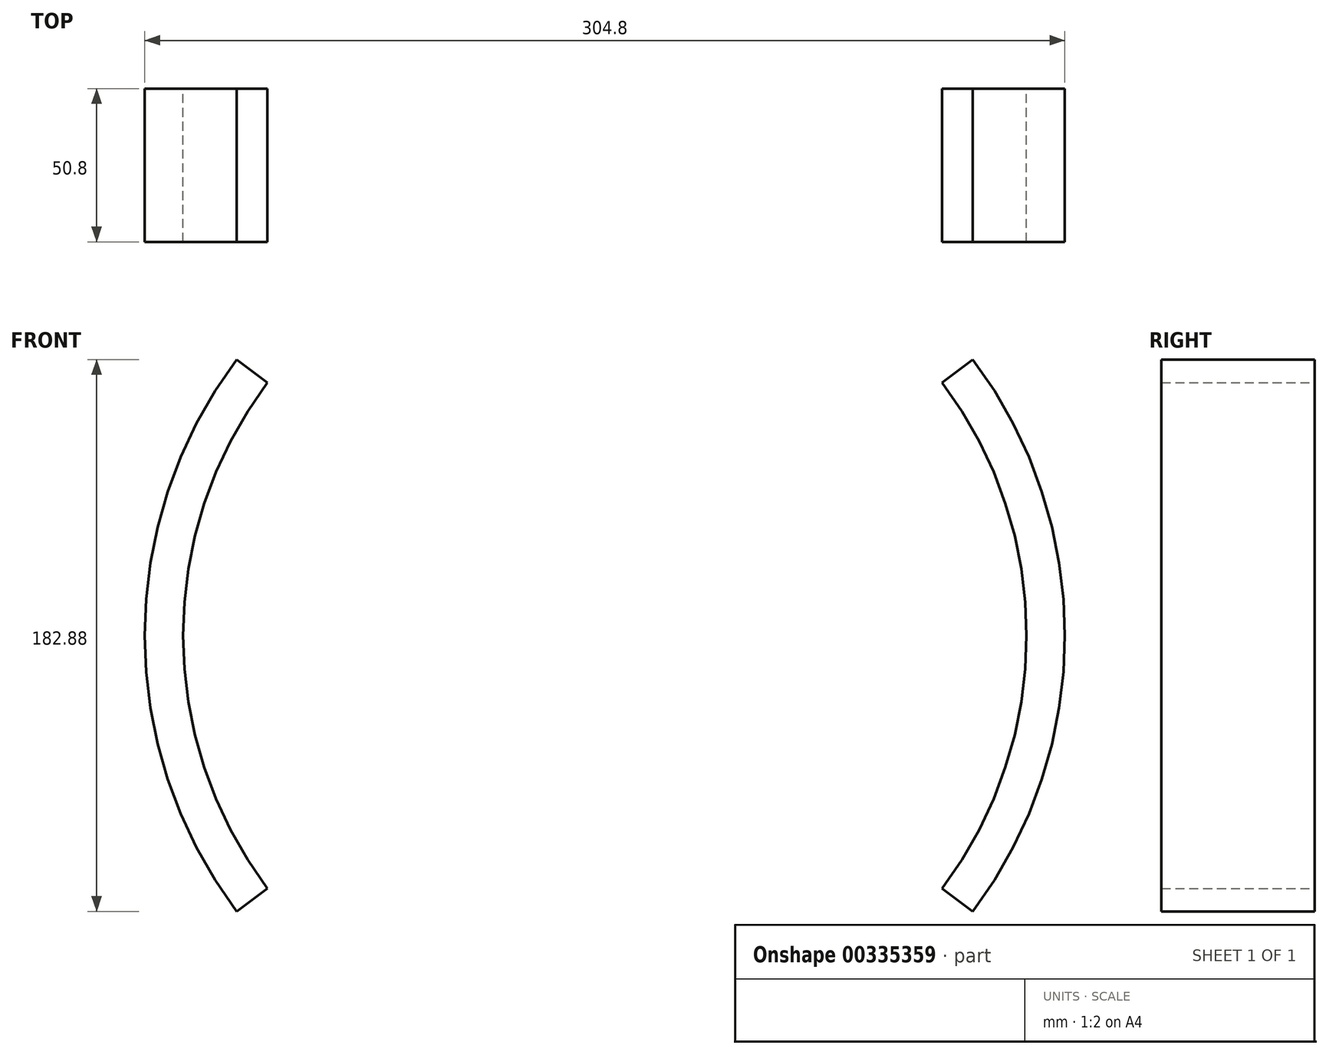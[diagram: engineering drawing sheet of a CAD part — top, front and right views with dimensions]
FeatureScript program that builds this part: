
annotation { "Feature Type Name" : "Feature", "Feature Type Description" : "" }
export const myFeature = defineFeature(function(context is Context, id is Id, definition is map)
    precondition{}
    {
        {
            var Q0;
            Q0=qCreatedBy(makeId("Front.planeOp"),FACE);
            var sketch = newSketch(context, id + "F0", { "sketchPlane" : qUnion([Q0])});
            skArc(sketch, "E0", {"start": v(111.76, -83.82) * mm, "mid": v(139.7, 0) * mm, "end": v(111.76, 83.82) * mm});
            skArc(sketch, "E1", {"start": v(121.92, -91.44) * mm, "mid": v(152.4, 0) * mm, "end": v(121.92, 91.44) * mm});
            skLineSegment(sketch, "E2", {"start": v(-152.4, 0) * mm, "end": v(-139.7, 0) * mm});
            skPoint(sketch, "E3", {"position": v(-111.76, 83.82) * mm});
            skPoint(sketch, "E4", {"position": v(-111.76, -83.82) * mm});
            skArc(sketch, "E5.trimOffspring", {"start": v(-111.76, 83.82) * mm, "mid": v(-139.7, 0) * mm, "end": v(-111.76, -83.82) * mm});
            skArc(sketch, "E6.trimOffspring", {"start": v(-121.92, 91.44) * mm, "mid": v(-152.4, 0) * mm, "end": v(-121.92, -91.44) * mm});
            skLineSegment(sketch, "E7.trimOffspring", {"start": v(-111.76, -83.82) * mm, "end": v(-121.92, -91.44) * mm});
            skLineSegment(sketch, "E8.trimOffspring", {"start": v(-111.76, 83.82) * mm, "end": v(-121.92, 91.44) * mm});
            skLineSegment(sketch, "E9.trimOffspring", {"start": v(139.7, 0) * mm, "end": v(152.4, 0) * mm});
            skLineSegment(sketch, "E10.trimOffspring", {"start": v(111.76, -83.82) * mm, "end": v(121.92, -91.44) * mm});
            skLineSegment(sketch, "E11.trimOffspring", {"start": v(111.76, 83.82) * mm, "end": v(121.92, 91.44) * mm});
            skSolve(sketch);
        }
        {
            var Q0;
            Q0 = qSketchRegion(id + "F0", true);
            extrude(context, id + "F1", {"entities" : qUnion([Q0]), "depth" : 50.8 * mm});
        }
    });
